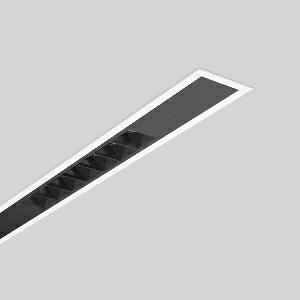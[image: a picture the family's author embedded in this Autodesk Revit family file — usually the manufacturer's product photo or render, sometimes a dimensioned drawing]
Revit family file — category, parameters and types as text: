
# Revit family: less_is_more_beamline_312469_002_1_76_222d
name_source: partatom
category: Lighting Fixtures
units: mm (PartAtom-declared; Revit-internal decimal feet)

## family parameters
Cut with Voids When Loaded = No
Host = Face
Light Source = No
Part Type = Normal
Room Calculation Point = No
Round Connector Dimension = Use Diameter
Shared = No

## types (1)
- LESS IS MORE BEAMLINE (1 x LED Modul 940, 1900 lm, 4000)
    Apparent Load = 48 VA
    CIE Flux Codes = 100 100 100 100 100
    Color Rendering = 92
    Color Temperature = 4000
    Default Elevation = 1800 mm
    Description = Series: LESS IS MORE BEAMLINE
Linear recessed ceiling and wall luminaire for aesthetically sophisticated lighting. Luminaire with two LED light units. Housing: extruded aluminium profile, powder-coated. End cap aluminium powder-coated. LED light unit with MRS technology: Mini-Reflector-System made of metallised thermoplastic with prismatic black glare-suppressing frame for pleasant glare-free light (RUG < 10). Each LED light unit has 7 reflector elements. Medium beam light distribution. Ceiling installation with pre-assembled SBS mounting system. LED unit with integrated converter interchangeable and removable. Suitable for through-wiring. 
Colour: traffic white, matt (RAL 9016)
Length: 1141 mm
Width: 71 mm
Height: 1.5 mm
Cut-out length: 1128 mm
Cut-out width: 60 mm
Recess height: 125 mm
Luminaire: recess height: 106 mm
Lamp: LED
Socket: without socket
Colour temperature: 4000K
Colour rendering index (CRI): 90
System power: 48 W
Rated luminous flux: 3800 lm
Luminous efficiency: 79 lm/W
Control gear: Converter, dimmable, DALI
Protection class: I
Type of protection: IP 20
    Height = 0 mm  [stored 0 ft]
    Lamp = 1 x LED Modul 940
    Lamp Light Flux = 1900 lm
    Lamp count = 1
    Length = 1141 mm
    Lifetime = 50000 h
    Luminous efficacy = 79 lm/W
    Manufacturer = RZB
    ModVariant = No
    Model = 312469.002.1.76
    Mounting Place = Ceiling, Wall
    Mounting Type = Recessed
    Number of Poles = 1
    OnlyDefault = Yes
    Power Factor = 1
    Product Name = LESS IS MORE BEAMLINE
    Product group = Recessed LED linear luminaires
    ProductGroupID = 407
    Protection Class = Protection class I
    Protection Degree = IP 20
    RLX_Detail_Level = 1
    RLX_Emergency_Light_Flux = 0 lm
    RLX_Emergency_Type = 0
    RLX_Emergency_Type_DB = No
    RlxData = <blob elided: 23769 chars, md5=926fee41>
    Socket = socket
    Standby Power = 0 W
    System Light Flux = 3800 lm
    System Power = 48 W
    Type Comments = Product without accessories
    Type Image = 312465.002.jpg
    URL = http://relux.com
    VarID = ---
    Voltage = 230 V
    Voltage Range = 220-240 V
    Weight = 0.00 kg
    Width = 71 mm

note: [stored X ft] marks values corroborated as IEEE doubles in the binary element streams (Revit-internal decimal feet)

## geometry (parser evidence)
native form markers: Blend x4, Sweep x16
no freeform markers — native parametric forms only
